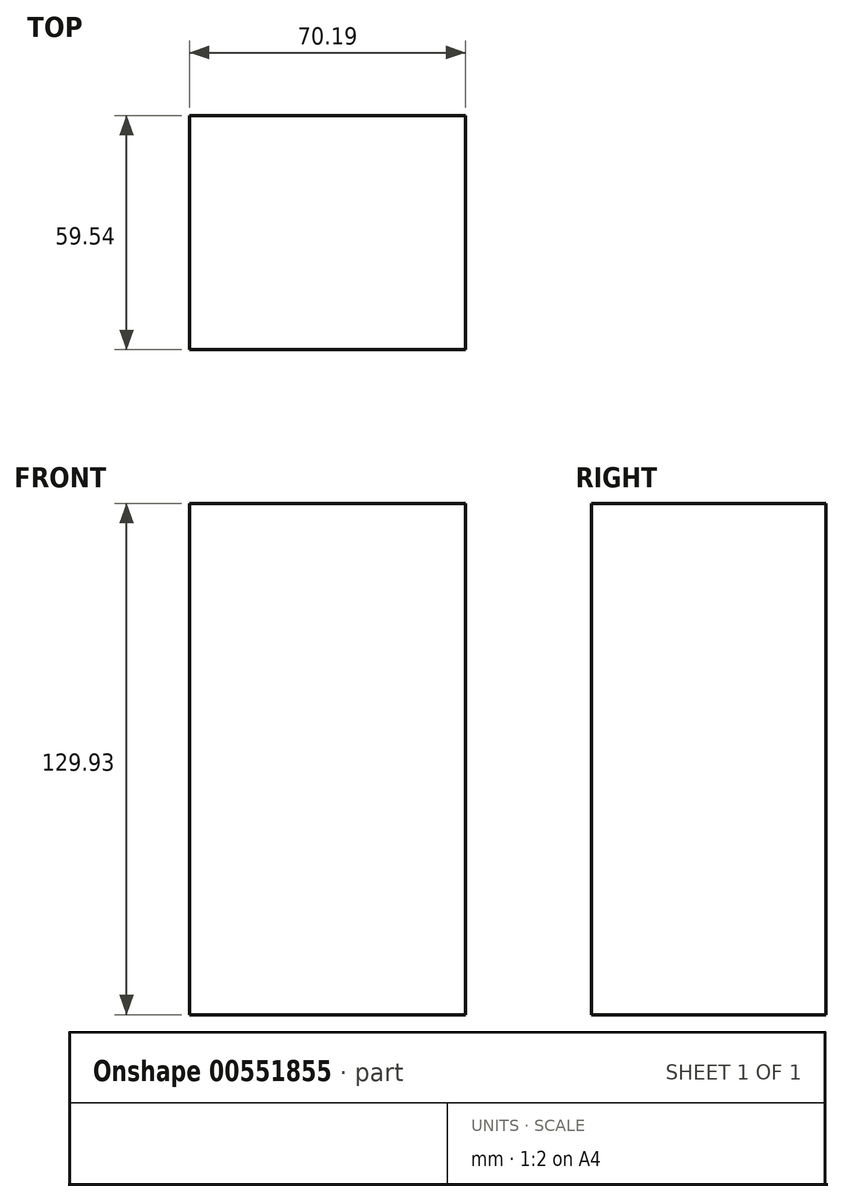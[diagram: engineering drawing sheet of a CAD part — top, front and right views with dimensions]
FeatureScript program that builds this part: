
annotation { "Feature Type Name" : "Feature", "Feature Type Description" : "" }
export const myFeature = defineFeature(function(context is Context, id is Id, definition is map)
    precondition{}
    {
        {
            var Q0;
            Q0=qCreatedBy(makeId("Top.planeOp"),FACE);
            var sketch = newSketch(context, id + "F0", { "sketchPlane" : qUnion([Q0])});
            skLineSegment(sketch, "E0.bottom", {"start": v(0, 9.45) * mm, "end": v(70.2, 9.45) * mm});
            skLineSegment(sketch, "E0.top", {"start": v(0, 69) * mm, "end": v(70.2, 69) * mm});
            skLineSegment(sketch, "E0.left", {"start": v(0, 9.45) * mm, "end": v(0, 69) * mm});
            skLineSegment(sketch, "E0.right", {"start": v(70.2, 9.45) * mm, "end": v(70.2, 69) * mm});
            skLineSegment(sketch, "E1.bottom", {"start": v(24.75, 69) * mm, "end": v(44.7, 69) * mm});
            skLineSegment(sketch, "E1.top", {"start": v(24.75, 69) * mm, "end": v(44.7, 69) * mm});
            skLineSegment(sketch, "E1.left", {"start": v(24.75, 69) * mm, "end": v(24.75, 69) * mm});
            skLineSegment(sketch, "E1.right", {"start": v(44.7, 69) * mm, "end": v(44.7, 69) * mm});
            skSolve(sketch);
        }
        {
            var Q0;
            Q0=makeQuery(id+"F0.imprint","IMPRINT",FACE,{"disambiguationData":[TD([[makeQuery(id+"F0.imprint","IMPRINT",EDGE,{"derivedFrom":sQuery(id+"F0.wireOp",EDGE,"E0.bottom")}),1.0]])]});
            extrude(context, id + "F1", {"entities" : qUnion([Q0]), "depth" : 129.93 * mm, "offsetDistance" : 25.4 * mm});
        }
        {
            var Q0;
            Q0=makeQuery(id+"F1.opExtrude","SWEPT_FACE",FACE,{"disambiguationData":[OSD([sQuery(id+"F0.wireOp",EDGE,"E0.right")])]});
            var sketch = newSketch(context, id + "F2", { "sketchPlane" : qUnion([Q0])});
            skLineSegment(sketch, "E2", {"start": v(9.45, 97.7) * mm, "end": v(23.55, 129.93) * mm});
            skLineSegment(sketch, "E3", {"start": v(23.55, 129.93) * mm, "end": v(69, 84.81) * mm});
            skLineSegment(sketch, "E4", {"start": v(69, 84.81) * mm, "end": v(54.73, 0) * mm});
            skLineSegment(sketch, "E5", {"start": v(54.73, 0) * mm, "end": v(9.45, 97.7) * mm});
            skSolve(sketch);
        }
        {
            var Q0;
            Q0 = qSketchRegion(id + "F2", true);
            extrude(context, id + "F3", {"entities" : qUnion([Q0]), "operationType" : NewBodyOperationType.ADD, "oppositeDirection" : true, "depth" : 69.56 * mm, "offsetDistance" : 25.4 * mm});
        }
    });
